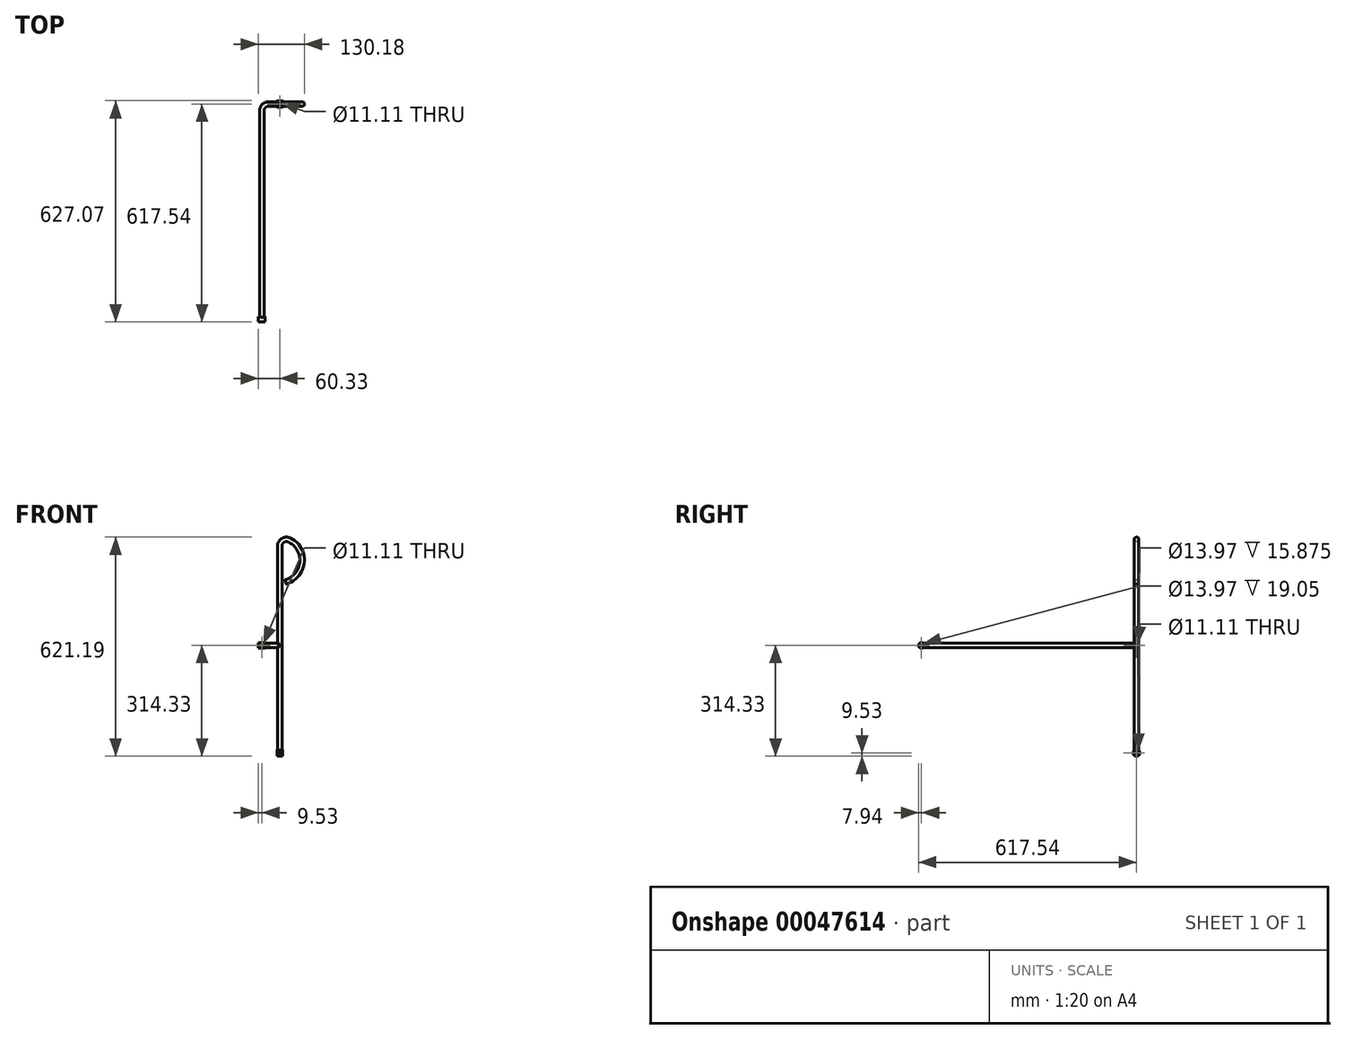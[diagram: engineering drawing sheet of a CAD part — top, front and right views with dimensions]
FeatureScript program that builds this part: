
annotation { "Feature Type Name" : "Feature", "Feature Type Description" : "" }
export const myFeature = defineFeature(function(context is Context, id is Id, definition is map)
    precondition{}
    {
        {
            var Q0;
            Q0=qCreatedBy(makeId("Front.planeOp"),FACE);
            var sketch = newSketch(context, id + "F0", { "sketchPlane" : qUnion([Q0])});
            skLineSegment(sketch, "E0", {"start": v(0, 0) * mm, "end": v(0, 586.26) * mm});
            skArc(sketch, "E1", {"start": v(16.44, 484.76) * mm, "mid": v(63.24, 540.36) * mm, "end": v(27.21, 603.47) * mm});
            skLineSegment(sketch, "E2", {"start": v(0, 546.1) * mm, "end": v(30.83, 431.05) * mm, "construction": true});
            skPoint(sketch, "E3.visualSharp", {"position": v(0, 609.6) * mm});
            skArc(sketch, "E3.filletArc", {"start": v(27.21, 603.47) * mm, "mid": v(8.87, 602.36) * mm, "end": v(0, 586.26) * mm});
            skSolve(sketch);
        }
        {
            var Q0;
            Q0=qCreatedBy(makeId("Top.planeOp"),FACE);
            var sketch = newSketch(context, id + "F1", { "sketchPlane" : qUnion([Q0])});
            skCircle(sketch, "E4", {"center": v(0, 0) * mm, "radius": 6.35 * mm});
            skCircle(sketch, "E5", {"center": v(0, 0) * mm, "radius": 5.56 * mm});
            skSolve(sketch);
        }
        {
            var Q0;
            Q0=qSketchRegion(id+"F1",true);
            var Q1;
            Q1=qConstructionFilter(qBodyType(qCreatedBy(id+"F0",EDGE),BodyType.WIRE),ConstructionObject.NO);
            sweep(context, id + "F2", {"profiles" : qUnion([Q0]), "path" : qUnion([Q1])});
        }
        {
            var Q0;
            Q0=makeQuery(id+"F2.opSweep","CAP_EDGE",EDGE,{"disambiguationData":[OSD([sQuery(id+"F0.wireOp",VERTEX,"E1.start"),sQuery(id+"F1.wireOp",EDGE,"E4")])],"isStart":false});
            chamfer(context, id + "F3", {"entities" : qUnion([Q0]), "width" : 0.8 * mm, "tangentPropagation" : true});
        }
        {
            var Q0;
            Q0=qCreatedBy(makeId("Right.planeOp"),FACE);
            var sketch = newSketch(context, id + "F4", { "sketchPlane" : qUnion([Q0])});
            skCircle(sketch, "E6", {"center": v(0, 0) * mm, "radius": 9.53 * mm});
            skSolve(sketch);
        }
        {
            var Q0;
            Q0=qSketchRegion(id+"F4",true);
            extrude(context, id + "F5", {"entities" : qUnion([Q0]), "operationType" : NewBodyOperationType.ADD, "depth" : 15.88 * mm, "hasDraft" : true, "draftAngle" : 3 * degree, "draftPullDirection" : true, "symmetric" : true});
        }
        {
            var Q0;
            Q0=makeQuery(id+"F5.opExtrude","CAP_FACE",FACE,{"disambiguationData":[OSD([sQuery(id+"F4.wireOp",EDGE,"E6")])],"isStart":false});
            var sketch = newSketch(context, id + "F6", { "sketchPlane" : qUnion([Q0])});
            skCircle(sketch, "E7", {"center": v(0, 0) * mm, "radius": 6.99 * mm});
            skSolve(sketch);
        }
        {
            var Q0;
            Q0=qSketchRegion(id+"F6",true);
            var Q1;
            Q1=makeQuery(id+"F5.opExtrude","CAP_FACE",FACE,{"disambiguationData":[OSD([sQuery(id+"F4.wireOp",EDGE,"E6")])],"isStart":true});
            extrude(context, id + "F7", {"entities" : qUnion([Q0]), "operationType" : NewBodyOperationType.REMOVE, "endBound" : BoundingType.UP_TO_SURFACE, "oppositeDirection" : true, "endBoundEntityFace" : qUnion([Q1]), "depth" : 25.4 * mm});
        }
        {
            var Q0;
            Q0=qCreatedBy(makeId("Right.planeOp"),FACE);
            var sketch = newSketch(context, id + "F8", { "sketchPlane" : qUnion([Q0])});
            skCircle(sketch, "E8", {"center": v(0, 304.8) * mm, "radius": 6.35 * mm});
            skCircle(sketch, "E9", {"center": v(0, 304.8) * mm, "radius": 5.56 * mm});
            skSolve(sketch);
        }
        {
            var Q0;
            Q0=qCreatedBy(makeId("Top.planeOp"),FACE);
            cPlane(context, id + "F9", {"entities" : qUnion([Q0]), "cplaneType" : CPlaneType.OFFSET, "offset" : 304.8 * mm, "width" : 152.4 * mm, "height" : 152.4 * mm});
        }
        {
            var Q0;
            Q0=qCreatedBy(id+"F9.planeOp",FACE);
            var sketch = newSketch(context, id + "F10", { "sketchPlane" : qUnion([Q0])});
            skLineSegment(sketch, "E10", {"start": v(0, 0) * mm, "end": v(-31.75, 0) * mm});
            skLineSegment(sketch, "E11", {"start": v(-50.8, -19.05) * mm, "end": v(-50.8, -609.6) * mm});
            skPoint(sketch, "E12.visualSharp", {"position": v(-50.8, 0) * mm});
            skArc(sketch, "E12.filletArc", {"start": v(-31.75, 0) * mm, "mid": v(-45.22, -5.58) * mm, "end": v(-50.8, -19.05) * mm});
            skSolve(sketch);
        }
        {
            var Q0;
            Q0=qSketchRegion(id+"F8",true);
            var Q1;
            Q1=qConstructionFilter(qBodyType(qCreatedBy(id+"F10",EDGE),BodyType.WIRE),ConstructionObject.NO);
            sweep(context, id + "F11", {"operationType" : NewBodyOperationType.ADD, "profiles" : qUnion([Q0]), "path" : qUnion([Q1])});
        }
        {
            var Q0;
            Q0=qCreatedBy(makeId("Right.planeOp"),FACE);
            cPlane(context, id + "F12", {"entities" : qUnion([Q0]), "cplaneType" : CPlaneType.OFFSET, "offset" : 50.8 * mm, "oppositeDirection" : true, "width" : 152.4 * mm, "height" : 152.4 * mm});
        }
        {
            var Q0;
            Q0=qCreatedBy(id+"F12.planeOp",FACE);
            var sketch = newSketch(context, id + "F13", { "sketchPlane" : qUnion([Q0])});
            skCircle(sketch, "E13", {"center": v(-609.6, 304.8) * mm, "radius": 7.94 * mm});
            skLineSegment(sketch, "E14", {"start": v(133.6, 304.8) * mm, "end": v(-690.42, 304.8) * mm, "construction": true});
            skLineSegment(sketch, "E15", {"start": v(0, 0) * mm, "end": v(0, 361.36) * mm, "construction": true});
            skSolve(sketch);
        }
        {
            var Q0;
            Q0=qSketchRegion(id+"F13",true);
            extrude(context, id + "F14", {"entities" : qUnion([Q0]), "operationType" : NewBodyOperationType.ADD, "depth" : 19.05 * mm, "symmetric" : true});
        }
        {
            var Q0;
            Q0=makeQuery(id+"F14.opExtrude","CAP_FACE",FACE,{"disambiguationData":[OSD([sQuery(id+"F13.wireOp",EDGE,"E13")])],"isStart":false});
            var sketch = newSketch(context, id + "F15", { "sketchPlane" : qUnion([Q0])});
            skCircle(sketch, "E16", {"center": v(-609.6, 304.8) * mm, "radius": 6.99 * mm});
            skSolve(sketch);
        }
        {
            var Q0;
            Q0=qSketchRegion(id+"F15",true);
            var Q1;
            Q1=makeQuery(id+"F14.opExtrude","CAP_FACE",FACE,{"disambiguationData":[OSD([sQuery(id+"F13.wireOp",EDGE,"E13")])],"isStart":true});
            extrude(context, id + "F16", {"entities" : qUnion([Q0]), "operationType" : NewBodyOperationType.REMOVE, "endBound" : BoundingType.UP_TO_SURFACE, "oppositeDirection" : true, "endBoundEntityFace" : qUnion([Q1]), "depth" : 25.4 * mm});
        }
    });
